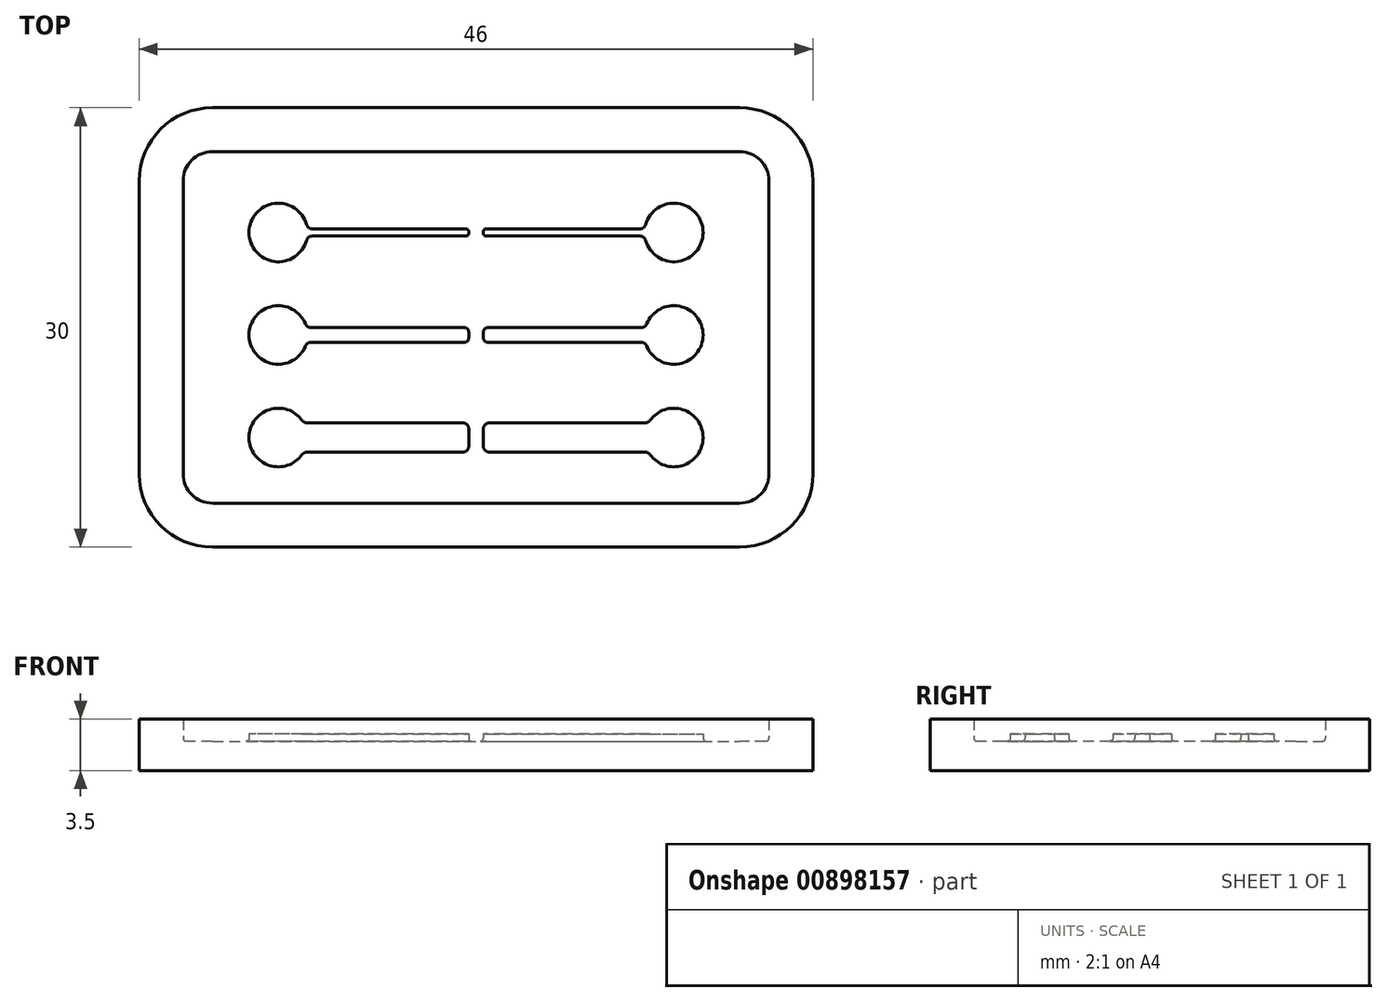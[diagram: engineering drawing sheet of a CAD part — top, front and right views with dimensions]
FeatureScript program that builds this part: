
annotation { "Feature Type Name" : "Feature", "Feature Type Description" : "" }
export const myFeature = defineFeature(function(context is Context, id is Id, definition is map)
    precondition{}
    {
        {
            var Q0;
            Q0=qCreatedBy(makeId("Top.planeOp"),FACE);
            var sketch = newSketch(context, id + "F0", { "sketchPlane" : qUnion([Q0])});
            skLineSegment(sketch, "E0", {"start": v(-16.1, 3.42) * mm, "end": v(-6.3, 3.42) * mm});
            skLineSegment(sketch, "E1", {"start": v(-6.1, 3.22) * mm, "end": v(-6.1, 3.17) * mm});
            skLineSegment(sketch, "E2", {"start": v(-6.1, 3.17) * mm, "end": v(-26.33, 3.17) * mm, "construction": true});
            skLineSegment(sketch, "E3.MirrorCS", {"start": v(-6.1, 3.12) * mm, "end": v(-6.1, 3.17) * mm});
            skLineSegment(sketch, "E4.MirrorCS", {"start": v(-16.1, 2.92) * mm, "end": v(-6.3, 2.92) * mm});
            skLineSegment(sketch, "E5", {"start": v(-5.6, 9.01) * mm, "end": v(-5.6, -3.31) * mm, "construction": true});
            skLineSegment(sketch, "E6", {"start": v(-6.1, -3.83) * mm, "end": v(-6.1, -3.63) * mm});
            skLineSegment(sketch, "E7", {"start": v(-6.4, -3.33) * mm, "end": v(-16.1, -3.33) * mm});
            skLineSegment(sketch, "E8", {"start": v(-21.1, -3.83) * mm, "end": v(-6.1, -3.83) * mm, "construction": true});
            skLineSegment(sketch, "E9", {"start": v(-6.5, -9.83) * mm, "end": v(-16.1, -9.83) * mm});
            skLineSegment(sketch, "E10.MirrorCS", {"start": v(-6.1, -3.83) * mm, "end": v(-6.1, -4.03) * mm});
            skLineSegment(sketch, "E11.MirrorCS", {"start": v(-6.4, -4.33) * mm, "end": v(-16.1, -4.33) * mm});
            skLineSegment(sketch, "E12.MirrorCS", {"start": v(-6.1, -10.83) * mm, "end": v(-6.1, -10.23) * mm});
            skLineSegment(sketch, "E13.MirrorCS", {"start": v(-6.5, -11.83) * mm, "end": v(-16.1, -11.83) * mm});
            skLineSegment(sketch, "E14.MirrorCS", {"start": v(-20.9, -10.83) * mm, "end": v(-5.9, -10.83) * mm, "construction": true});
            skLineSegment(sketch, "E15.MirrorCS", {"start": v(-6.1, -10.83) * mm, "end": v(-6.1, -11.43) * mm});
            skArc(sketch, "E16", {"start": v(-17.18, 3.71) * mm, "mid": v(-21.1, 3.17) * mm, "end": v(-17.18, 2.63) * mm});
            skLineSegment(sketch, "E17", {"start": v(-16.1, 3.42) * mm, "end": v(-16.8, 3.42) * mm});
            skLineSegment(sketch, "E18", {"start": v(-16.1, 2.92) * mm, "end": v(-16.8, 2.92) * mm});
            skLineSegment(sketch, "E19.MirrorCS", {"start": v(-5.1, 3.12) * mm, "end": v(-5.1, 3.17) * mm});
            skLineSegment(sketch, "E20.MirrorCS", {"start": v(-5.1, 3.22) * mm, "end": v(-5.1, 3.17) * mm});
            skLineSegment(sketch, "E21.MirrorCS", {"start": v(4.9, 2.92) * mm, "end": v(-4.9, 2.92) * mm});
            skArc(sketch, "E22.MirrorCS", {"start": v(5.97, 3.71) * mm, "mid": v(9.9, 3.17) * mm, "end": v(5.97, 2.63) * mm});
            skLineSegment(sketch, "E23.MirrorCS", {"start": v(4.9, 3.42) * mm, "end": v(-4.9, 3.42) * mm});
            skLineSegment(sketch, "E24.MirrorCS", {"start": v(4.9, 3.42) * mm, "end": v(5.58, 3.42) * mm});
            skLineSegment(sketch, "E25.MirrorCS", {"start": v(4.9, 2.92) * mm, "end": v(5.58, 2.92) * mm});
            skPoint(sketch, "E26.visualSharp", {"position": v(-6.1, 3.42) * mm});
            skArc(sketch, "E26.filletArc", {"start": v(-6.1, 3.22) * mm, "mid": v(-6.17, 3.36) * mm, "end": v(-6.3, 3.42) * mm});
            skPoint(sketch, "E27.visualSharp", {"position": v(-6.1, 2.92) * mm});
            skArc(sketch, "E27.filletArc", {"start": v(-6.3, 2.92) * mm, "mid": v(-6.17, 2.98) * mm, "end": v(-6.1, 3.12) * mm});
            skPoint(sketch, "E28.visualSharp", {"position": v(-5.1, 3.42) * mm});
            skArc(sketch, "E28.filletArc", {"start": v(-4.9, 3.42) * mm, "mid": v(-5.05, 3.36) * mm, "end": v(-5.1, 3.22) * mm});
            skPoint(sketch, "E29.visualSharp", {"position": v(-5.1, 2.92) * mm});
            skArc(sketch, "E29.filletArc", {"start": v(-5.1, 3.12) * mm, "mid": v(-5.05, 2.98) * mm, "end": v(-4.9, 2.92) * mm});
            skPoint(sketch, "E30.visualSharp", {"position": v(-6.1, -3.33) * mm});
            skArc(sketch, "E30.filletArc", {"start": v(-6.1, -3.63) * mm, "mid": v(-6.2, -3.42) * mm, "end": v(-6.4, -3.33) * mm});
            skPoint(sketch, "E31.visualSharp", {"position": v(-6.1, -4.33) * mm});
            skArc(sketch, "E31.filletArc", {"start": v(-6.4, -4.33) * mm, "mid": v(-6.2, -4.24) * mm, "end": v(-6.1, -4.03) * mm});
            skArc(sketch, "E32", {"start": v(-17.25, -3.08) * mm, "mid": v(-21.1, -3.83) * mm, "end": v(-17.25, -4.58) * mm});
            skLineSegment(sketch, "E33", {"start": v(-16.1, -3.33) * mm, "end": v(-16.88, -3.33) * mm});
            skLineSegment(sketch, "E34", {"start": v(-16.1, -4.33) * mm, "end": v(-16.88, -4.33) * mm});
            skArc(sketch, "E35", {"start": v(-17.48, -9.66) * mm, "mid": v(-21.1, -10.83) * mm, "end": v(-17.48, -12) * mm});
            skLineSegment(sketch, "E36", {"start": v(-16.1, -9.83) * mm, "end": v(-17.16, -9.83) * mm});
            skLineSegment(sketch, "E37", {"start": v(-16.1, -11.83) * mm, "end": v(-17.16, -11.83) * mm});
            skPoint(sketch, "E38.visualSharp", {"position": v(-6.1, -9.83) * mm});
            skArc(sketch, "E38.filletArc", {"start": v(-6.1, -10.23) * mm, "mid": v(-6.22, -9.95) * mm, "end": v(-6.5, -9.83) * mm});
            skPoint(sketch, "E39.visualSharp", {"position": v(-6.1, -11.83) * mm});
            skArc(sketch, "E39.filletArc", {"start": v(-6.5, -11.83) * mm, "mid": v(-6.22, -11.71) * mm, "end": v(-6.1, -11.43) * mm});
            skPoint(sketch, "E40.visualSharp", {"position": v(-17.37, -9.83) * mm});
            skArc(sketch, "E40.filletArc", {"start": v(-17.48, -9.66) * mm, "mid": v(-17.34, -9.78) * mm, "end": v(-17.16, -9.83) * mm});
            skPoint(sketch, "E41.visualSharp", {"position": v(-17.37, -11.83) * mm});
            skArc(sketch, "E41.filletArc", {"start": v(-17.16, -11.83) * mm, "mid": v(-17.34, -11.87) * mm, "end": v(-17.48, -12) * mm});
            skPoint(sketch, "E42.visualSharp", {"position": v(-17.17, -4.33) * mm});
            skArc(sketch, "E42.filletArc", {"start": v(-16.88, -4.33) * mm, "mid": v(-17.1, -4.4) * mm, "end": v(-17.25, -4.58) * mm});
            skPoint(sketch, "E43.visualSharp", {"position": v(-17.17, -3.33) * mm});
            skArc(sketch, "E43.filletArc", {"start": v(-17.25, -3.08) * mm, "mid": v(-17.1, -3.26) * mm, "end": v(-16.88, -3.33) * mm});
            skPoint(sketch, "E44.visualSharp", {"position": v(-17.12, 2.92) * mm});
            skArc(sketch, "E44.filletArc", {"start": v(-16.8, 2.92) * mm, "mid": v(-17.04, 2.84) * mm, "end": v(-17.18, 2.63) * mm});
            skPoint(sketch, "E45.visualSharp", {"position": v(-17.12, 3.42) * mm});
            skArc(sketch, "E45.filletArc", {"start": v(-17.18, 3.71) * mm, "mid": v(-17.04, 3.5) * mm, "end": v(-16.8, 3.42) * mm});
            skPoint(sketch, "E46.visualSharp", {"position": v(5.9, 3.42) * mm});
            skArc(sketch, "E46.filletArc", {"start": v(5.58, 3.42) * mm, "mid": v(5.82, 3.5) * mm, "end": v(5.97, 3.71) * mm});
            skPoint(sketch, "E47.visualSharp", {"position": v(5.9, 2.92) * mm});
            skArc(sketch, "E47.filletArc", {"start": v(5.97, 2.63) * mm, "mid": v(5.82, 2.84) * mm, "end": v(5.58, 2.92) * mm});
            skLineSegment(sketch, "E48.MirrorCS", {"start": v(-5.1, -3.83) * mm, "end": v(-5.1, -3.63) * mm});
            skLineSegment(sketch, "E49.MirrorCS", {"start": v(-5.1, -3.83) * mm, "end": v(-5.1, -4.03) * mm});
            skArc(sketch, "E50.MirrorCS", {"start": v(5.94, -11.83) * mm, "mid": v(6.13, -11.87) * mm, "end": v(6.27, -12) * mm});
            skArc(sketch, "E51.MirrorCS", {"start": v(-5.1, -3.63) * mm, "mid": v(-5.02, -3.42) * mm, "end": v(-4.8, -3.33) * mm});
            skArc(sketch, "E52.MirrorCS", {"start": v(6.04, -3.08) * mm, "mid": v(5.9, -3.26) * mm, "end": v(5.67, -3.33) * mm});
            skArc(sketch, "E53.MirrorCS", {"start": v(6.27, -9.66) * mm, "mid": v(6.13, -9.78) * mm, "end": v(5.94, -9.83) * mm});
            skArc(sketch, "E54.MirrorCS", {"start": v(5.67, -4.33) * mm, "mid": v(5.9, -4.4) * mm, "end": v(6.04, -4.58) * mm});
            skArc(sketch, "E55.MirrorCS", {"start": v(-4.8, -4.33) * mm, "mid": v(-5.02, -4.24) * mm, "end": v(-5.1, -4.03) * mm});
            skLineSegment(sketch, "E56.MirrorCS", {"start": v(4.9, -4.33) * mm, "end": v(5.67, -4.33) * mm});
            skLineSegment(sketch, "E57.MirrorCS", {"start": v(4.9, -3.33) * mm, "end": v(5.67, -3.33) * mm});
            skLineSegment(sketch, "E58.MirrorCS", {"start": v(-5.1, -10.83) * mm, "end": v(-5.1, -10.23) * mm});
            skArc(sketch, "E59.MirrorCS", {"start": v(-5.1, -10.23) * mm, "mid": v(-4.99, -9.95) * mm, "end": v(-4.7, -9.83) * mm});
            skLineSegment(sketch, "E60.MirrorCS", {"start": v(-5.1, -10.83) * mm, "end": v(-5.1, -11.43) * mm});
            skArc(sketch, "E61.MirrorCS", {"start": v(-4.7, -11.83) * mm, "mid": v(-4.99, -11.71) * mm, "end": v(-5.1, -11.43) * mm});
            skArc(sketch, "E62.MirrorCS", {"start": v(6.04, -3.08) * mm, "mid": v(9.9, -3.83) * mm, "end": v(6.04, -4.58) * mm});
            skPoint(sketch, "E63.MirrorP", {"position": v(-5.1, -11.83) * mm});
            skPoint(sketch, "E64.MirrorP", {"position": v(-5.1, -3.33) * mm});
            skLineSegment(sketch, "E65.MirrorCS", {"start": v(-4.7, -11.83) * mm, "end": v(4.9, -11.83) * mm});
            skPoint(sketch, "E66.MirrorP", {"position": v(-5.1, -4.33) * mm});
            skLineSegment(sketch, "E67.MirrorCS", {"start": v(-4.8, -3.33) * mm, "end": v(4.9, -3.33) * mm});
            skPoint(sketch, "E68.MirrorP", {"position": v(6.16, -9.83) * mm});
            skLineSegment(sketch, "E69.MirrorCS", {"start": v(9.68, -10.83) * mm, "end": v(-5.32, -10.83) * mm, "construction": true});
            skLineSegment(sketch, "E70.MirrorCS", {"start": v(9.9, -3.83) * mm, "end": v(-5.1, -3.83) * mm, "construction": true});
            skLineSegment(sketch, "E71.MirrorCS", {"start": v(-4.7, -9.83) * mm, "end": v(4.9, -9.83) * mm});
            skLineSegment(sketch, "E72.MirrorCS", {"start": v(4.9, -9.83) * mm, "end": v(5.94, -9.83) * mm});
            skLineSegment(sketch, "E73.MirrorCS", {"start": v(-4.8, -4.33) * mm, "end": v(4.9, -4.33) * mm});
            skPoint(sketch, "E74.MirrorP", {"position": v(-5.1, -9.83) * mm});
            skLineSegment(sketch, "E75.MirrorCS", {"start": v(4.9, -11.83) * mm, "end": v(5.94, -11.83) * mm});
            skPoint(sketch, "E76.MirrorP", {"position": v(5.96, -3.33) * mm});
            skPoint(sketch, "E77.MirrorP", {"position": v(6.16, -11.83) * mm});
            skPoint(sketch, "E78.MirrorP", {"position": v(5.96, -4.33) * mm});
            skArc(sketch, "E79.MirrorCS", {"start": v(6.27, -9.66) * mm, "mid": v(9.9, -10.83) * mm, "end": v(6.27, -12) * mm});
            skSolve(sketch);
        }
        {
            var Q0;
            Q0=qCreatedBy(makeId("Top.planeOp"),FACE);
            var sketch = newSketch(context, id + "F1", { "sketchPlane" : qUnion([Q0])});
            skLineSegment(sketch, "E80.0", {"start": v(-5.6, 9.01) * mm, "end": v(-5.6, -3.31) * mm, "construction": true});
            skLineSegment(sketch, "E81", {"start": v(-5.6, 8.69) * mm, "end": v(-25.6, 8.69) * mm});
            skLineSegment(sketch, "E82", {"start": v(-25.6, 8.69) * mm, "end": v(-25.6, -3.31) * mm});
            skLineSegment(sketch, "E83.MirrorCS", {"start": v(14.4, 8.69) * mm, "end": v(14.4, -3.31) * mm});
            skLineSegment(sketch, "E84.MirrorCS", {"start": v(-5.6, 8.69) * mm, "end": v(14.4, 8.69) * mm});
            skLineSegment(sketch, "E85", {"start": v(-25.6, -3.31) * mm, "end": v(14.4, -3.31) * mm, "construction": true});
            skLineSegment(sketch, "E86.MirrorCS", {"start": v(-5.6, -15.31) * mm, "end": v(-25.6, -15.31) * mm});
            skLineSegment(sketch, "E87.MirrorCS", {"start": v(-25.6, -15.31) * mm, "end": v(-25.6, -3.31) * mm});
            skLineSegment(sketch, "E88.MirrorCS", {"start": v(-5.6, -15.31) * mm, "end": v(14.4, -15.31) * mm});
            skLineSegment(sketch, "E89.MirrorCS", {"start": v(14.4, -15.31) * mm, "end": v(14.4, -3.31) * mm});
            skSolve(sketch);
        }
        {
            var Q0;
            Q0 = qSketchRegion(id + "F1", true);
            extrude(context, id + "F2", {"entities" : qUnion([Q0]), "oppositeDirection" : true, "depth" : 2 * mm, "offsetDistance" : 25 * mm});
        }
        {
            var Q0;
            Q0=makeQuery(id+"F2.opExtrude","SWEPT_EDGE",EDGE,{"disambiguationData":[OSD([sQuery(id+"F1.wireOp",EDGE,"E86.MirrorCS"),sQuery(id+"F1.wireOp",EDGE,"E87.MirrorCS")])]});
            var Q1;
            Q1=makeQuery(id+"F2.opExtrude","SWEPT_EDGE",EDGE,{"disambiguationData":[OSD([sQuery(id+"F1.wireOp",EDGE,"E88.MirrorCS"),sQuery(id+"F1.wireOp",EDGE,"E89.MirrorCS")])]});
            var Q2;
            Q2=makeQuery(id+"F2.opExtrude","SWEPT_EDGE",EDGE,{"disambiguationData":[OSD([sQuery(id+"F1.wireOp",EDGE,"E83.MirrorCS"),sQuery(id+"F1.wireOp",EDGE,"E84.MirrorCS")])]});
            var Q3;
            Q3=makeQuery(id+"F2.opExtrude","SWEPT_EDGE",EDGE,{"disambiguationData":[OSD([sQuery(id+"F1.wireOp",EDGE,"E81"),sQuery(id+"F1.wireOp",EDGE,"E82")])]});
            fillet(context, id + "F3", {"entities" : qUnion([Q0, Q1, Q2, Q3]), "radius" : 2 * mm, "tangentPropagation" : true, "allowEdgeOverflow" : false});
        }
        {
            var Q0;
            Q0 = qSketchRegion(id + "F0", true);
            extrude(context, id + "F4", {"entities" : qUnion([Q0]), "operationType" : NewBodyOperationType.ADD, "depth" : 0.5 * mm, "offsetDistance" : 25 * mm});
        }
        {
            var Q0;
            Q0=makeQuery(id+"F2.opExtrude","CAP_FACE",FACE,{"disambiguationData":[OSD([sQuery(id+"F1.wireOp",EDGE,"E81"),sQuery(id+"F1.wireOp",EDGE,"E82"),sQuery(id+"F1.wireOp",EDGE,"E83.MirrorCS"),sQuery(id+"F1.wireOp",EDGE,"E84.MirrorCS"),sQuery(id+"F1.wireOp",EDGE,"E86.MirrorCS"),sQuery(id+"F1.wireOp",EDGE,"E87.MirrorCS"),sQuery(id+"F1.wireOp",EDGE,"E88.MirrorCS"),sQuery(id+"F1.wireOp",EDGE,"E89.MirrorCS")])],"isStart":false});
            var sketch = newSketch(context, id + "F5", { "sketchPlane" : qUnion([Q0])});
            skLineSegment(sketch, "E90.0", {"start": v(-23.6, 18.31) * mm, "end": v(12.4, 18.31) * mm});
            skArc(sketch, "E90.1", {"start": v(17.4, 13.31) * mm, "mid": v(15.93, 16.85) * mm, "end": v(12.4, 18.31) * mm});
            skArc(sketch, "E90.2", {"start": v(-23.6, 18.31) * mm, "mid": v(-27.14, 16.85) * mm, "end": v(-28.6, 13.31) * mm});
            skLineSegment(sketch, "E90.3", {"start": v(17.4, 13.31) * mm, "end": v(17.4, -6.69) * mm});
            skLineSegment(sketch, "E90.4", {"start": v(-28.6, -6.69) * mm, "end": v(-28.6, 13.31) * mm});
            skArc(sketch, "E90.5", {"start": v(-28.6, -6.69) * mm, "mid": v(-27.14, -10.22) * mm, "end": v(-23.6, -11.69) * mm});
            skLineSegment(sketch, "E90.6", {"start": v(-23.6, -11.69) * mm, "end": v(12.4, -11.69) * mm});
            skArc(sketch, "E90.7", {"start": v(12.4, -11.69) * mm, "mid": v(15.93, -10.22) * mm, "end": v(17.4, -6.69) * mm});
            skSolve(sketch);
        }
        {
            var Q0;
            Q0=makeQuery(id+"F5.imprint","IMPRINT",FACE,{"disambiguationData":[TD([[makeQuery(id+"F5.imprint","IMPRINT",EDGE,{"derivedFrom":sQuery(id+"F5.wireOp",EDGE,"E90.0")}),-1.0]])]});
            extrude(context, id + "F6", {"entities" : qUnion([Q0]), "operationType" : NewBodyOperationType.ADD, "oppositeDirection" : true, "depth" : 3.5 * mm, "offsetDistance" : 25 * mm});
        }
        {
            var Q0;
            Q0=makeQuery(id+"F2.opExtrude","CAP_FACE",FACE,{"disambiguationData":[OSD([sQuery(id+"F1.wireOp",EDGE,"E81"),sQuery(id+"F1.wireOp",EDGE,"E82"),sQuery(id+"F1.wireOp",EDGE,"E83.MirrorCS"),sQuery(id+"F1.wireOp",EDGE,"E84.MirrorCS"),sQuery(id+"F1.wireOp",EDGE,"E86.MirrorCS"),sQuery(id+"F1.wireOp",EDGE,"E87.MirrorCS"),sQuery(id+"F1.wireOp",EDGE,"E88.MirrorCS"),sQuery(id+"F1.wireOp",EDGE,"E89.MirrorCS")])],"isStart":true});
            fillet(context, id + "F7", {"entities" : qUnion([Q0]), "radius" : 0.2 * mm, "tangentPropagation" : true, "allowEdgeOverflow" : false});
        }
    });
